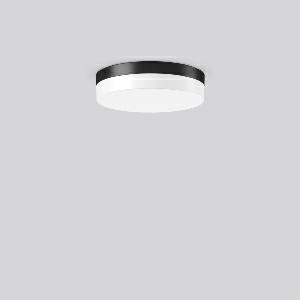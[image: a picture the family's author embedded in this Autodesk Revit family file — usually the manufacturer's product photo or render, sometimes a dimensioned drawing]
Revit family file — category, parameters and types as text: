
# Revit family: flat_slim_round_312629_0031_19_bc5e
name_source: partatom
category: Lighting Fixtures
units: mm (PartAtom-declared; Revit-internal decimal feet)

## family parameters
Cut with Voids When Loaded = No
Host = Face
Light Source = No
Part Type = Normal
Room Calculation Point = No
Round Connector Dimension = Use Diameter
Shared = No

## types (1)
- MultiLumen 1 830 (1 x LED Modul 830, 1250 lm, 3000)
    Apparent Load = 13 VA
    CIE Flux Codes = 38 68 89 82 100
    Color Rendering = 80
    Color Temperature = 3000
    Default Elevation = 1800 mm
    Height = 75 mm
    Lamp = 1 x LED Modul 830
    Lamp Light Flux = 1250 lm
    Lamp count = 1
    Length = 300 mm
    Lifetime = 50000 h
    Luminous efficacy = 96 lm/W
    Manufacturer = RZB
    ModVariant = No
    Model = 312629.0031.19
    Mounting Place = Ceiling
    Mounting Type = Surface mounted
    Number of Poles = 1
    OnlyDefault = Yes
    Power Factor = 1
    Product Name = FLAT SLIM round
    Product group = Surface mounted ceiling and wall luminaires
    ProductGroupID = 305
    Protection Class = Protection class I
    Protection Degree = Degree of protection
    RLX_Detail_Level = 1
    RLX_Emergency_Light_Flux = 0 lm
    RLX_Emergency_Type = 0
    RLX_Emergency_Type_DB = No
    RlxData = <blob elided: 18109 chars, md5=913d513d>
    Socket = socket
    Standby Power = 0 W
    System Light Flux = 1250 lm
    System Power = 13 W
    Type Comments = MultiLumen 1 830
    Type Image = 312629.0031.jpg
    URL = http://relux.com
    VarID = multilumen_1_830
    Voltage = 0 V
    Weight = 0.00 kg
    Width = 0 mm  [stored 0 ft]

note: [stored X ft] marks values corroborated as IEEE doubles in the binary element streams (Revit-internal decimal feet)

## geometry (parser evidence)
native form markers: Blend x4, Sweep x14
no freeform markers — native parametric forms only
